# Revit family: Distanzmuffe rund VA
name_source: partatom
category: HLS-Bauteile
revit_build: Autodesk Revit 2017 (Build: 20190507_1515(x64)
units: mm (PartAtom-declared; Revit-internal decimal feet)

## family parameters
Arbeitsebenenbasiert = Nein
Beim Laden mit Abzugskörper schneiden = Nein
Bemaßung runder Anschluss = Durchmesser verwenden
Gemeinsam genutzt = Ja
Immer vertikal = Nein
Raumberechnungspunkt = Nein
Teiletyp = Normal

## types (4) — shared parameters
Fabrikat = MEFA
Kurztext1 = Distanzmuffe rund V2A
Material = Edelstahl
Mengeneinheit = St

## per-type parameters (varying)
| type | Artikelnummer | D | D0 | EAN | Gewicht | Gewicht pro Bauteil | Kurztext2 | Länge | vpe |
| Distanzmuffe rund M 8 L= 30, V2A | 0700025 | 11 mm  [stored 0.0360892 ft] | 7 mm  [stored 0.0229659 ft] | 4250928415981 | 0.01 kg | 0.01 kg | Innengew. M8 L= 30 mm | 30 mm  [stored 0.0984252 ft] | 100 St |
| Distanzmuffe rund M10 L= 40, V2A | 0700026 | 13 mm | 8 mm  [stored 0.0262467 ft] | 4250928415998 | 0.02 kg | 0.02 kg | Innengew. M10 L= 40 mm | 40 mm  [stored 0.131234 ft] | 50 St |
| Distanzmuffe rund M12 L= 40, V2A | 0700027 | 15 mm  [stored 0.0492126 ft] | 10 mm  [stored 0.0328084 ft] | 4250928416001 | 0.03 kg | 0.03 kg | Innengew. M12 L= 40 mm | 40 mm  [stored 0.131234 ft] | 50 St |
| Distanzmuffe rund M16 L= 50, V2A | 0700028 | 22 mm  [stored 0.0721785 ft] | 14 mm  [stored 0.0459318 ft] | 4250928416018 | 0.09 kg | 0.09 kg | Innengew. M16 L= 50 mm | 50 mm  [stored 0.164042 ft] | 25 St |

note: [stored X ft] marks values corroborated as IEEE doubles in the binary element streams (Revit-internal decimal feet)
